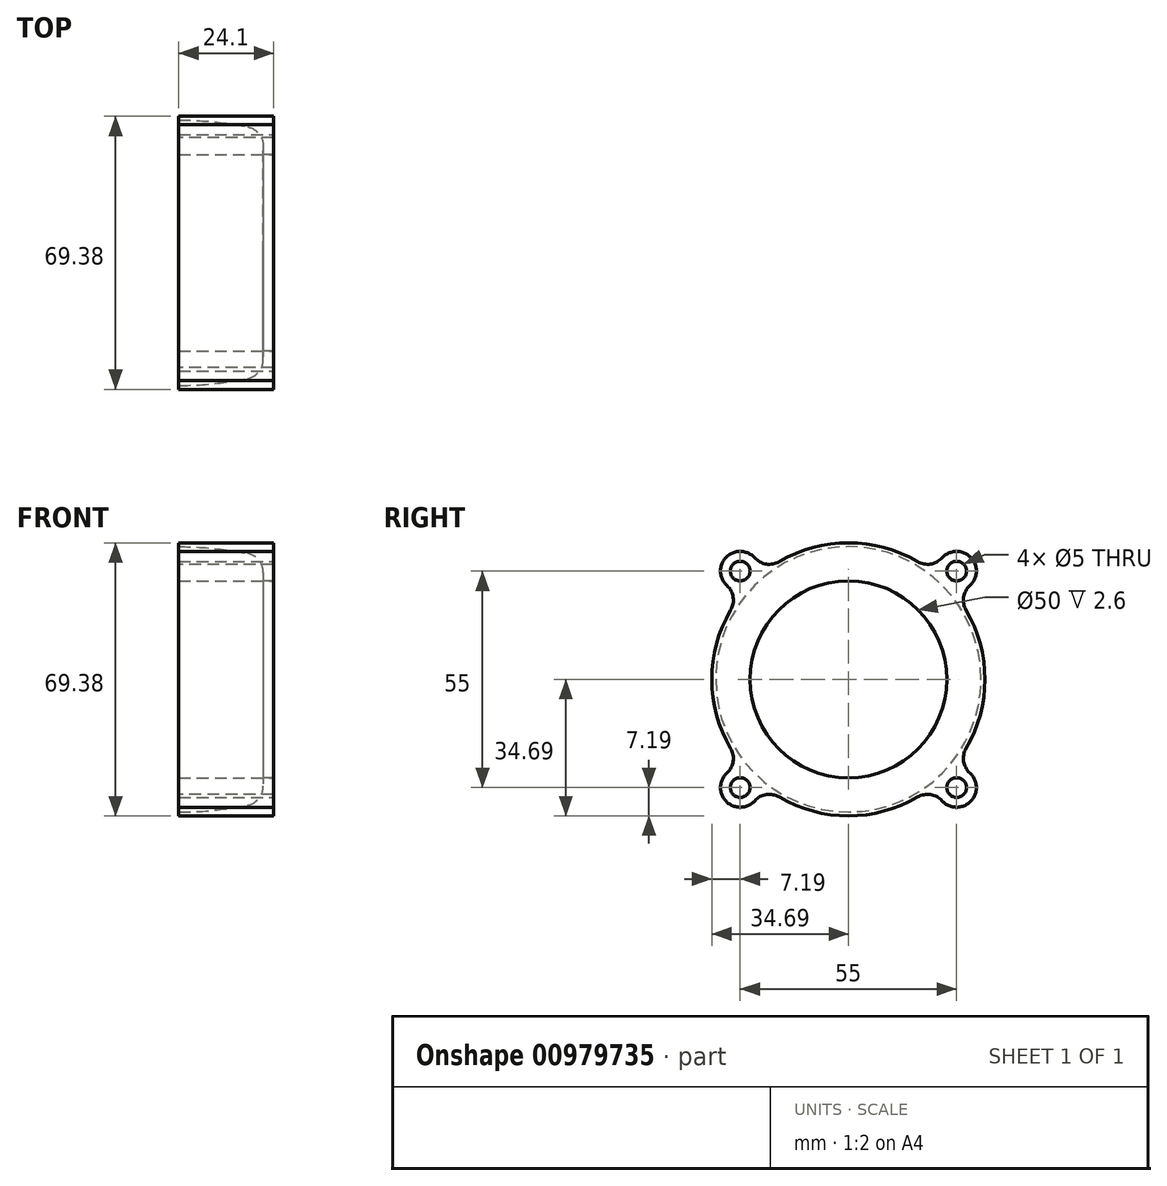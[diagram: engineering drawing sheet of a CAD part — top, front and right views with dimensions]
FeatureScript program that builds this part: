
annotation { "Feature Type Name" : "Feature", "Feature Type Description" : "" }
export const myFeature = defineFeature(function(context is Context, id is Id, definition is map)
    precondition{}
    {
        {
            var Q0;
            Q0=qCreatedBy(makeId("Front.planeOp"),FACE);
            var sketch = newSketch(context, id + "F0", { "sketchPlane" : qUnion([Q0])});
            skLineSegment(sketch, "E0.bottom", {"start": v(24.1, 40) * mm, "end": v(-24.1, 40) * mm});
            skLineSegment(sketch, "E0.top", {"start": v(24.1, -40) * mm, "end": v(-24.1, -40) * mm});
            skLineSegment(sketch, "E0.left", {"start": v(24.1, 40) * mm, "end": v(24.1, -40) * mm});
            skLineSegment(sketch, "E0.right", {"start": v(-24.1, 40) * mm, "end": v(-24.1, -40) * mm});
            skPoint(sketch, "E0.middle", {"position": v(0, 0) * mm});
            skSolve(sketch);
        }
        {
            var Q0;
            Q0 = qSketchRegion(id + "F0", true);
            extrude(context, id + "F1", {"entities" : qUnion([Q0]), "depth" : 40 * mm, "offsetDistance" : 25 * mm, "hasSecondDirection" : true, "secondDirectionOppositeDirection" : true, "secondDirectionDepth" : 40 * mm});
        }
        {
            var Q0;
            Q0=qCreatedBy(makeId("Front.planeOp"),FACE);
            var sketch = newSketch(context, id + "F2", { "sketchPlane" : qUnion([Q0])});
            skLineSegment(sketch, "E1.left", {"start": v(-21.5, 25) * mm, "end": v(-21.5, 27.1) * mm});
            skPoint(sketch, "E2.center.orphan", {"position": v(0, -56.3) * mm});
            skPoint(sketch, "E3.start.orphan", {"position": v(-44.08, 0) * mm});
            skArc(sketch, "E4", {"start": v(17.47, 32) * mm, "mid": v(0, 33.7) * mm, "end": v(-17.47, 32) * mm});
            skLineSegment(sketch, "E5", {"start": v(21.5, 27.1) * mm, "end": v(21.5, 25) * mm});
            skArc(sketch, "E6", {"start": v(-17.47, 32) * mm, "mid": v(-20.36, 30.26) * mm, "end": v(-21.5, 27.1) * mm});
            skArc(sketch, "E7", {"start": v(21.5, 27.1) * mm, "mid": v(20.36, 30.26) * mm, "end": v(17.47, 32) * mm});
            skLineSegment(sketch, "E8", {"start": v(-44.08, 0) * mm, "end": v(-21.5, 0) * mm, "construction": true});
            skPoint(sketch, "E9.middle", {"position": v(0, 0) * mm});
            skPoint(sketch, "E9.top.end.orphan", {"position": v(-16.5, -33.27) * mm});
            skPoint(sketch, "E10.orphan", {"position": v(12.4, -25) * mm});
            skLineSegment(sketch, "E11.trimOffspring", {"start": v(21.5, 0) * mm, "end": v(38.47, 0) * mm, "construction": true});
            skPoint(sketch, "E12.start.orphan", {"position": v(-12.4, 25) * mm});
            skPoint(sketch, "E13.start.orphan", {"position": v(16.5, 33.27) * mm});
            skLineSegment(sketch, "E14", {"start": v(-21.5, 0) * mm, "end": v(21.5, 0) * mm});
            skLineSegment(sketch, "E15.bottom", {"start": v(-38.47, 25) * mm, "end": v(38.47, 25) * mm});
            skLineSegment(sketch, "E15.left", {"start": v(-38.47, 25) * mm, "end": v(-38.47, 0) * mm});
            skLineSegment(sketch, "E15.right", {"start": v(38.47, 25) * mm, "end": v(38.47, 0) * mm});
            skLineSegment(sketch, "E16", {"start": v(-38.47, 0) * mm, "end": v(38.47, 0) * mm});
            skPoint(sketch, "E15.top.start.orphan", {"position": v(-38.47, -25) * mm});
            skPoint(sketch, "E17.orphan", {"position": v(38.47, -25) * mm});
            skSolve(sketch);
        }
        {
            var Q0;
            Q0=qSketchRegion(id+"F2",true);
            var Q1;
            Q1=sQuery(id+"F2.wireOp",EDGE,"E8");
            revolve(context, id + "F3", {"operationType" : NewBodyOperationType.REMOVE, "surfaceOperationType" : NewSurfaceOperationType.NEW, "entities" : qUnion([Q0]), "axis" : qUnion([Q1]), "revolveType" : RevolveType.FULL});
        }
        {
            var Q0;
            Q0=makeQuery(id+"F1.opExtrude","SWEPT_FACE",FACE,{"disambiguationData":[OSD([sQuery(id+"F0.wireOp",EDGE,"E0.left")])]});
            var sketch = newSketch(context, id + "F4", { "sketchPlane" : qUnion([Q0])});
            skArc(sketch, "E18", {"start": v(-26.27, -22.65) * mm, "mid": v(-31.04, -31.04) * mm, "end": v(-22.65, -26.27) * mm});
            skArc(sketch, "E19", {"start": v(-22.65, 26.27) * mm, "mid": v(-31.04, 31.04) * mm, "end": v(-26.27, 22.65) * mm});
            skArc(sketch, "E20", {"start": v(26.27, 22.65) * mm, "mid": v(31.04, 31.04) * mm, "end": v(22.65, 26.27) * mm});
            skArc(sketch, "E21", {"start": v(22.65, -26.27) * mm, "mid": v(31.04, -31.04) * mm, "end": v(26.27, -22.65) * mm});
            skArc(sketch, "E22", {"start": v(-22.65, -26.27) * mm, "mid": v(0, -34.69) * mm, "end": v(22.65, -26.27) * mm});
            skArc(sketch, "E23.trimOffspring", {"start": v(-26.27, 22.65) * mm, "mid": v(-34.69, 0) * mm, "end": v(-26.27, -22.65) * mm});
            skArc(sketch, "E24.trimOffspring", {"start": v(22.65, 26.27) * mm, "mid": v(0, 34.69) * mm, "end": v(-22.65, 26.27) * mm});
            skArc(sketch, "E25.trimOffspring", {"start": v(26.27, -22.65) * mm, "mid": v(34.69, 0) * mm, "end": v(26.27, 22.65) * mm});
            skCircle(sketch, "E26", {"center": v(0, 0) * mm, "radius": 64.28 * mm});
            skSolve(sketch);
        }
        {
            var Q0;
            Q0 = qSketchRegion(id + "F4", true);
            extrude(context, id + "F5", {"entities" : qUnion([Q0]), "operationType" : NewBodyOperationType.REMOVE, "oppositeDirection" : true, "depth" : 40 * mm, "offsetDistance" : 25 * mm});
        }
        {
            var Q0;
            Q0=makeQuery(id+"F5.boolean.opBoolean","MERGE",FACE,{"derivedFrom":[makeQuery(id+"F1.opExtrude","SWEPT_FACE",FACE,{"disambiguationData":[OSD([sQuery(id+"F0.wireOp",EDGE,"E0.left")])]}),makeQuery(id+"F5.opExtrude","CAP_FACE",FACE,{"disambiguationData":[OSD([sQuery(id+"F4.wireOp",EDGE,"E18")])],"isStart":true}),makeQuery(id+"F5.opExtrude","CAP_FACE",FACE,{"disambiguationData":[OSD([sQuery(id+"F4.wireOp",EDGE,"E19")])],"isStart":true}),makeQuery(id+"F5.opExtrude","CAP_FACE",FACE,{"disambiguationData":[OSD([sQuery(id+"F4.wireOp",EDGE,"E20")])],"isStart":true}),makeQuery(id+"F5.opExtrude","CAP_FACE",FACE,{"disambiguationData":[OSD([sQuery(id+"F4.wireOp",EDGE,"E21")])],"isStart":true})]});
            var sketch = newSketch(context, id + "F6", { "sketchPlane" : qUnion([Q0])});
            skCircle(sketch, "E27", {"center": v(-27.5, 27.5) * mm, "radius": 2.5 * mm});
            skCircle(sketch, "E28", {"center": v(27.5, 27.5) * mm, "radius": 2.5 * mm});
            skCircle(sketch, "E29", {"center": v(-27.5, -27.5) * mm, "radius": 2.5 * mm});
            skCircle(sketch, "E30", {"center": v(27.5, -27.5) * mm, "radius": 2.5 * mm});
            skSolve(sketch);
        }
        {
            var Q0;
            Q0 = qSketchRegion(id + "F6", true);
            extrude(context, id + "F7", {"entities" : qUnion([Q0]), "operationType" : NewBodyOperationType.REMOVE, "endBound" : BoundingType.THROUGH_ALL, "oppositeDirection" : true, "depth" : 25 * mm, "offsetDistance" : 25 * mm});
        }
        {
            var Q0;
            Q0=qCreatedBy(makeId("Right.planeOp"),FACE);
            var sketch = newSketch(context, id + "F8", { "sketchPlane" : qUnion([Q0])});
            skLineSegment(sketch, "E31.bottom", {"start": v(-50, -50) * mm, "end": v(50, -50) * mm});
            skLineSegment(sketch, "E31.top", {"start": v(-50, 50) * mm, "end": v(50, 50) * mm});
            skLineSegment(sketch, "E31.left", {"start": v(-50, -50) * mm, "end": v(-50, 50) * mm});
            skLineSegment(sketch, "E31.right", {"start": v(50, -50) * mm, "end": v(50, 50) * mm});
            skPoint(sketch, "E31.middle", {"position": v(0, 0) * mm});
            skSolve(sketch);
        }
        {
            var Q0;
            Q0 = qSketchRegion(id + "F8", true);
            extrude(context, id + "F9", {"entities" : qUnion([Q0]), "operationType" : NewBodyOperationType.REMOVE, "endBound" : BoundingType.THROUGH_ALL, "oppositeDirection" : true, "depth" : 25 * mm, "offsetDistance" : 25 * mm});
        }
        {
            var Q0;
            Q0=makeQuery(id+"F5.boolean.opBoolean","COPY",EDGE,{"derivedFrom":makeQuery(id+"F5.opExtrude","SWEPT_EDGE",EDGE,{"disambiguationData":[OSD([sQuery(id+"F4.wireOp",EDGE,"E18"),sQuery(id+"F4.wireOp",EDGE,"E23.trimOffspring")])]})});
            var Q1;
            Q1=makeQuery(id+"F5.boolean.opBoolean","COPY",EDGE,{"derivedFrom":makeQuery(id+"F5.opExtrude","SWEPT_EDGE",EDGE,{"disambiguationData":[OSD([sQuery(id+"F4.wireOp",EDGE,"E19"),sQuery(id+"F4.wireOp",EDGE,"E23.trimOffspring")])]})});
            var Q2;
            Q2=makeQuery(id+"F5.boolean.opBoolean","COPY",EDGE,{"derivedFrom":makeQuery(id+"F5.opExtrude","SWEPT_EDGE",EDGE,{"disambiguationData":[OSD([sQuery(id+"F4.wireOp",EDGE,"E20"),sQuery(id+"F4.wireOp",EDGE,"E24.trimOffspring")])]})});
            var Q3;
            Q3=makeQuery(id+"F5.boolean.opBoolean","COPY",EDGE,{"derivedFrom":makeQuery(id+"F5.opExtrude","SWEPT_EDGE",EDGE,{"disambiguationData":[OSD([sQuery(id+"F4.wireOp",EDGE,"E19"),sQuery(id+"F4.wireOp",EDGE,"E24.trimOffspring")])]})});
            var Q4;
            Q4=makeQuery(id+"F5.boolean.opBoolean","COPY",EDGE,{"derivedFrom":makeQuery(id+"F5.opExtrude","SWEPT_EDGE",EDGE,{"disambiguationData":[OSD([sQuery(id+"F4.wireOp",EDGE,"E20"),sQuery(id+"F4.wireOp",EDGE,"E25.trimOffspring")])]})});
            var Q5;
            Q5=makeQuery(id+"F5.boolean.opBoolean","COPY",EDGE,{"derivedFrom":makeQuery(id+"F5.opExtrude","SWEPT_EDGE",EDGE,{"disambiguationData":[OSD([sQuery(id+"F4.wireOp",EDGE,"E21"),sQuery(id+"F4.wireOp",EDGE,"E25.trimOffspring")])]})});
            var Q6;
            Q6=makeQuery(id+"F5.boolean.opBoolean","COPY",EDGE,{"derivedFrom":makeQuery(id+"F5.opExtrude","SWEPT_EDGE",EDGE,{"disambiguationData":[OSD([sQuery(id+"F4.wireOp",EDGE,"E21"),sQuery(id+"F4.wireOp",EDGE,"E22")])]})});
            var Q7;
            Q7=makeQuery(id+"F5.boolean.opBoolean","COPY",EDGE,{"derivedFrom":makeQuery(id+"F5.opExtrude","SWEPT_EDGE",EDGE,{"disambiguationData":[OSD([sQuery(id+"F4.wireOp",EDGE,"E18"),sQuery(id+"F4.wireOp",EDGE,"E22")])]})});
            fillet(context, id + "F10", {"entities" : qUnion([Q0, Q1, Q2, Q3, Q4, Q5, Q6, Q7]), "radius" : 5 * mm, "tangentPropagation" : true, "allowEdgeOverflow" : false});
        }
    });
